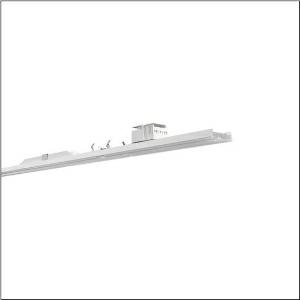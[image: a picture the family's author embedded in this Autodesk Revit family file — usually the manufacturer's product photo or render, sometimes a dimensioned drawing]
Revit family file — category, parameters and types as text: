
# Revit family: licross_r__11_recessed_mo_51tl18dv48xf_e9bc
name_source: partatom
category: Lighting Fixtures
units: mm (PartAtom-declared; Revit-internal decimal feet)

## family parameters
Cut with Voids When Loaded = No
Host = Face
Light Source = No
Part Type = Normal
Room Calculation Point = No
Round Connector Dimension = Use Diameter
Shared = No

## types (1)
- --- (1 x LED, 8000 lm, 45.5 W, 4000K)
    Apparent Load = 46 VA
    CIE Flux Codes = 83 96 99 100 100
    Color Rendering = 80
    Color Temperature = 4000K
    Default Elevation = 1800 mm
    Description = Licross® 11 Recessed MOluminaire insert, length: 2.250mm, width: 66mm, height: 67mm, LED rated luminous flux: 8.000lm, light colour: 840, control gear: DALI 2, control gear: ECG DALI, with plug, 5-pole, with phase selection, mains connection: 220..240V, AC, 50/60Hz, halogen-free wiring, primary optical cover: cover, of PMMA, light emission: direct distribution, protection rating (complete): IP40, insulation class (complete): insulation class I (protective earthing), certification: CE, ENEC, VDE, protection symbol: D if used in an environment without relevant dust loads with corresponding accessories, permissible ambient temperature for indoor applications: -25..+45°C, corresponds to IFS (International Featured Standards) requirements for safety and quality in the food industry, reducing of maximum allowable ambient temperature of 5°C with ceiling mounting, packaging unit: 1 piece
    Height = 58 mm
    Lamp = 1 x LED
    Lamp Light Flux = 8000 lm
    Lamp Power = 45.5 W
    Lamp count = 1
    Length = 2250 mm
    Luminous efficacy = 176 lm/W
    Manufacturer = Siteco
    ModVariant = No
    Model = 51TL18DV48XF
    Mounting Place = Ceiling
    Mounting Type = Pendant
    Number of Poles = 1
    OnlyDefault = Yes
    Power Factor = 1
    Product Name = Licross® 11 Recessed MO
    Product group = luminaire insert
    ProductGroupID = 902
    Protection Class = Protection class I
    Protection Degree = IP 40
    RLX_Detail_Level = 1
    RlxData = <blob elided: 27145 chars, md5=0f1a974d>
    Socket = socket
    Standby Power = 0 W
    System Light Flux = 8000 lm
    System Power = 46 W
    Type Comments = factory setting: luminous flux: 100 % | dim-lin: 254 | 205 mA
    Type Image = l_1266722.jpg
    URL = http://relux.com
    VarID = @adj_133078
    Voltage = 0 V
    Weight = 0.00 kg
    Width = 66 mm

## geometry (parser evidence)
native form markers: Blend x4, Sweep x10
no freeform markers — native parametric forms only
